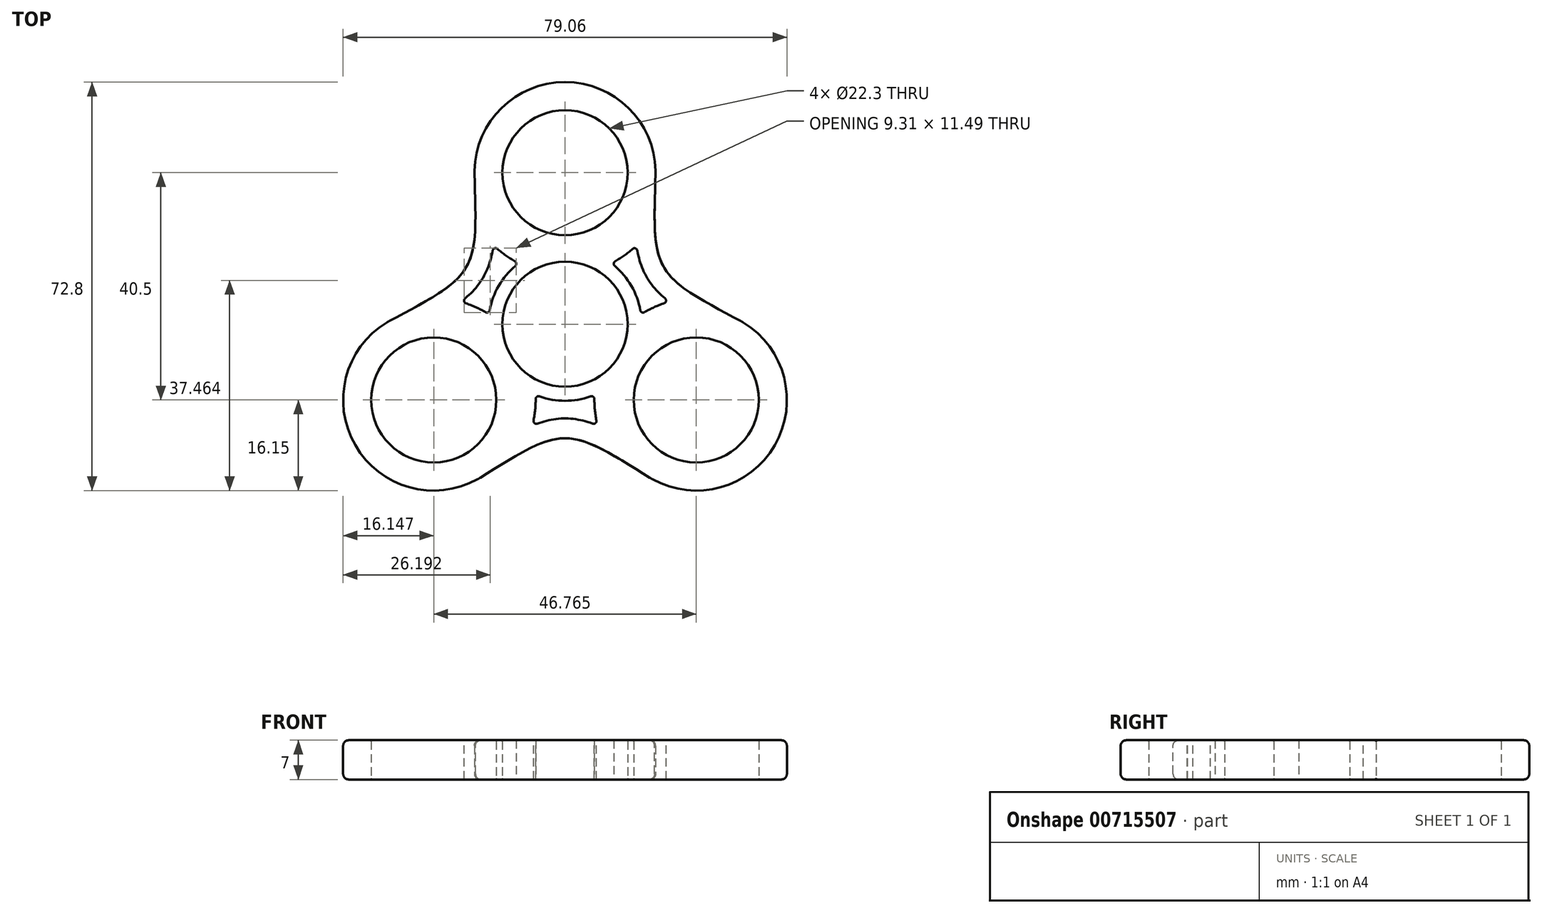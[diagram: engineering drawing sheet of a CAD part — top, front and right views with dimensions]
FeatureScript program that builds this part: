
annotation { "Feature Type Name" : "Feature", "Feature Type Description" : "" }
export const myFeature = defineFeature(function(context is Context, id is Id, definition is map)
    precondition{}
    {
        {
            var Q0;
            Q0=qCreatedBy(makeId("Top.planeOp"),FACE);
            var sketch = newSketch(context, id + "F0", { "sketchPlane" : qUnion([Q0])});
            skCircle(sketch, "E0", {"center": v(0, 0) * mm, "radius": 11.15 * mm});
            skLineSegment(sketch, "E1.0", {"start": v(-15.15, 0) * mm, "end": v(-15.15, 0) * mm});
            skLineSegment(sketch, "E2", {"start": v(0, 0) * mm, "end": v(0, 27) * mm, "construction": true});
            skCircle(sketch, "E3", {"center": v(0, 27) * mm, "radius": 11.15 * mm});
            skArc(sketch, "E4.0", {"start": v(16.15, 27) * mm, "mid": v(0, 43.15) * mm, "end": v(-16.15, 27) * mm});
            skLineSegment(sketch, "E5", {"start": v(-15.15, 0) * mm, "end": v(15.15, 0) * mm, "construction": true});
            skLineSegment(sketch, "E6", {"start": v(-16.15, 27) * mm, "end": v(16.15, 27) * mm, "construction": true});
            skPoint(sketch, "E7.trimOffspring.end.orphan", {"position": v(-15.15, 0) * mm});
            skLineSegment(sketch, "E8", {"start": v(-16.15, 27) * mm, "end": v(-16.15, 27) * mm});
            skArc(sketch, "E9.trimOffspring", {"start": v(-15.15, 0) * mm, "mid": v(0, -15.15) * mm, "end": v(15.15, 0) * mm, "construction": true});
            skLineSegment(sketch, "E10.trimOffspring", {"start": v(16.15, 27) * mm, "end": v(16.15, 27) * mm});
            skLineSegment(sketch, "E11.anchor1", {"start": v(0, 27) * mm, "end": v(0, 43.15) * mm, "construction": true});
            skLineSegment(sketch, "E11.anchor2", {"start": v(0, 27) * mm, "end": v(13.23, 36.26) * mm, "construction": true});
            skLineSegment(sketch, "E12.1.0", {"start": v(7.57, -13.12) * mm, "end": v(-7.58, 13.12) * mm, "construction": true});
            skLineSegment(sketch, "E12.1.2", {"start": v(0, 0) * mm, "end": v(-23.38, -13.5) * mm, "construction": true});
            skLineSegment(sketch, "E12.1.4", {"start": v(-15.3, -27.49) * mm, "end": v(-31.46, 0.49) * mm, "construction": true});
            skCircle(sketch, "E12.1.5", {"center": v(-23.38, -13.5) * mm, "radius": 11.15 * mm});
            skPoint(sketch, "E12.1.9", {"position": v(7.57, -13.12) * mm});
            skArc(sketch, "E12.1.14", {"start": v(-31.46, 0.49) * mm, "mid": v(-37.37, -21.57) * mm, "end": v(-15.3, -27.49) * mm});
            skLineSegment(sketch, "E12.2.0", {"start": v(7.57, 13.12) * mm, "end": v(-7.58, -13.12) * mm, "construction": true});
            skLineSegment(sketch, "E12.2.2", {"start": v(0, 0) * mm, "end": v(23.38, -13.5) * mm, "construction": true});
            skLineSegment(sketch, "E12.2.4", {"start": v(31.46, 0.49) * mm, "end": v(15.3, -27.49) * mm, "construction": true});
            skCircle(sketch, "E12.2.5", {"center": v(23.38, -13.5) * mm, "radius": 11.15 * mm});
            skArc(sketch, "E12.2.12", {"start": v(7.57, 13.12) * mm, "mid": v(-13.12, 7.57) * mm, "end": v(-7.58, -13.12) * mm, "construction": true});
            skArc(sketch, "E12.2.14", {"start": v(15.3, -27.49) * mm, "mid": v(37.37, -21.57) * mm, "end": v(31.46, 0.49) * mm});
            skFitSpline(sketch, "E13", {"points": [v(16.15, 27) * mm, v(31.46, 0.49) * mm], "startDerivative": vector(-1.87, -54.1) * mm, "endDerivative": vector(47.8, -25.43) * mm});
            skLineSegment(sketch, "E14", {"start": v(0, 0) * mm, "end": v(26.97, 15.57) * mm, "construction": true});
            skLineSegment(sketch, "E15", {"start": v(-15.3, -27.49) * mm, "end": v(-3.01, -11.46) * mm});
            skLineSegment(sketch, "E16", {"start": v(-3.01, -11.46) * mm, "end": v(3.36, -11.46) * mm});
            skLineSegment(sketch, "E17", {"start": v(3.36, -11.46) * mm, "end": v(15.3, -27.49) * mm});
            skLineSegment(sketch, "E18", {"start": v(-31.46, 0.49) * mm, "end": v(-13.47, 2.14) * mm});
            skLineSegment(sketch, "E19", {"start": v(-13.47, 2.14) * mm, "end": v(-9.18, 9.2) * mm});
            skLineSegment(sketch, "E20", {"start": v(-9.18, 9.2) * mm, "end": v(-16.15, 27) * mm});
            skSolve(sketch);
        }
        {
            var Q0;
            Q0=qCreatedBy(makeId("Right.planeOp"),FACE);
            var sketch = newSketch(context, id + "F1", { "sketchPlane" : qUnion([Q0])});
            skLineSegment(sketch, "E21", {"start": v(0, 18.91) * mm, "end": v(0, -18.72) * mm, "construction": true});
            skSolve(sketch);
        }
        {
            var Q0;
            Q0=makeQuery(id+"F0.imprint","IMPRINT",FACE,{"disambiguationData":[TD([[makeQuery(id+"F0.imprint","IMPRINT",EDGE,{"derivedFrom":sQuery(id+"F0.wireOp",EDGE,"E0")}),-1.0]])]});
            var Q1;
            Q1=makeQuery(id+"F0.imprint","IMPRINT",FACE,{"disambiguationData":[TD([[makeQuery(id+"F0.imprint","IMPRINT",EDGE,{"derivedFrom":sQuery(id+"F0.wireOp",EDGE,"E3")}),-1.0]])]});
            extrude(context, id + "F2", {"entities" : qUnion([Q0, Q1]), "depth" : 7 * mm, "offsetDistance" : 25 * mm});
        }
        {
            var Q0;
            Q0=makeQuery(id+"F2.opExtrude","SWEPT_BODY",BODY,{"disambiguationData":[OSD([sQuery(id+"F0.wireOp",EDGE,"E0"),sQuery(id+"F0.wireOp",EDGE,"E1.0"),sQuery(id+"F0.wireOp",EDGE,"E3"),sQuery(id+"F0.wireOp",EDGE,"E4.0"),sQuery(id+"F0.wireOp",EDGE,"oIW5whhO-fQ4n-saJ2-gWf4-q0JPziCMkqRt"),sQuery(id+"F0.wireOp",EDGE,"e7664bf7-e720-472f-93c8-efa73fce652a0.MirrorCS"),sQuery(id+"F0.wireOp",EDGE,"15db0cb3-5bd8-46cc-a881-ea2e00802e11.filletArc"),sQuery(id+"F0.wireOp",EDGE,"163ba6b5-26b9-4c58-8659-ca6763b85cf9.filletArc")])]});
            var Q1;
            Q1=sQuery(id+"F1.wireOp",EDGE,"E21");
            circularPattern(context, id + "F3", {"operationType" : NewBodyOperationType.ADD, "entities" : qUnion([Q0]), "axis" : qUnion([Q1]), "angle" : 360 * degree, "instanceCount" : 3, "equalSpace" : true});
        }
        {
            var Q0;
            Q0=makeQuery(id+"F2.opExtrude","SWEPT_EDGE",EDGE,{"disambiguationData":[OSD([sQuery(id+"F0.wireOp",EDGE,"E4.0"),sQuery(id+"F0.wireOp",EDGE,"E13")])]});
            var Q1;
            Q1=makeQuery(id+"F2.opExtrude","SWEPT_EDGE",EDGE,{"disambiguationData":[OSD([sQuery(id+"F0.wireOp",EDGE,"E12.2.14"),sQuery(id+"F0.wireOp",EDGE,"E13")])]});
            var Q2;
            Q2=makeQuery(id+"F3.boolean.opBoolean","MERGE",EDGE,{"derivedFrom":[makeQuery(id+"F2.opExtrude","SWEPT_EDGE",EDGE,{"disambiguationData":[OSD([sQuery(id+"F0.wireOp",EDGE,"E12.2.14"),sQuery(id+"F0.wireOp",EDGE,"E17")])]}),makeQuery(id+"F3.opPattern","COPY",EDGE,{"derivedFrom":makeQuery(id+"F2.opExtrude","SWEPT_EDGE",EDGE,{"disambiguationData":[OSD([sQuery(id+"F0.wireOp",EDGE,"E4.0"),sQuery(id+"F0.wireOp",EDGE,"E13")])]}),"instanceName":"1"})]});
            var Q3;
            Q3=makeQuery(id+"F3.boolean.opBoolean","MERGE",EDGE,{"derivedFrom":[makeQuery(id+"F2.opExtrude","SWEPT_EDGE",EDGE,{"disambiguationData":[OSD([sQuery(id+"F0.wireOp",EDGE,"E12.1.14"),sQuery(id+"F0.wireOp",EDGE,"E15")])]}),makeQuery(id+"F3.opPattern","COPY",EDGE,{"derivedFrom":makeQuery(id+"F2.opExtrude","SWEPT_EDGE",EDGE,{"disambiguationData":[OSD([sQuery(id+"F0.wireOp",EDGE,"E12.2.14"),sQuery(id+"F0.wireOp",EDGE,"E13")])]}),"instanceName":"1"})]});
            var Q4;
            Q4=makeQuery(id+"F3.boolean.opBoolean","MERGE",EDGE,{"derivedFrom":[makeQuery(id+"F2.opExtrude","SWEPT_EDGE",EDGE,{"disambiguationData":[OSD([sQuery(id+"F0.wireOp",EDGE,"E12.1.14"),sQuery(id+"F0.wireOp",EDGE,"E18")])]}),makeQuery(id+"F3.opPattern","COPY",EDGE,{"derivedFrom":makeQuery(id+"F2.opExtrude","SWEPT_EDGE",EDGE,{"disambiguationData":[OSD([sQuery(id+"F0.wireOp",EDGE,"E12.2.14"),sQuery(id+"F0.wireOp",EDGE,"E17")])]}),"instanceName":"1"}),makeQuery(id+"F3.opPattern","COPY",EDGE,{"derivedFrom":makeQuery(id+"F2.opExtrude","SWEPT_EDGE",EDGE,{"disambiguationData":[OSD([sQuery(id+"F0.wireOp",EDGE,"E4.0"),sQuery(id+"F0.wireOp",EDGE,"E13")])]}),"instanceName":"2"})]});
            var Q5;
            Q5=makeQuery(id+"F3.boolean.opBoolean","MERGE",EDGE,{"derivedFrom":[makeQuery(id+"F2.opExtrude","SWEPT_EDGE",EDGE,{"disambiguationData":[OSD([sQuery(id+"F0.wireOp",EDGE,"E4.0"),sQuery(id+"F0.wireOp",EDGE,"E20")])]}),makeQuery(id+"F3.opPattern","COPY",EDGE,{"derivedFrom":makeQuery(id+"F2.opExtrude","SWEPT_EDGE",EDGE,{"disambiguationData":[OSD([sQuery(id+"F0.wireOp",EDGE,"E12.1.14"),sQuery(id+"F0.wireOp",EDGE,"E15")])]}),"instanceName":"1"}),makeQuery(id+"F3.opPattern","COPY",EDGE,{"derivedFrom":makeQuery(id+"F2.opExtrude","SWEPT_EDGE",EDGE,{"disambiguationData":[OSD([sQuery(id+"F0.wireOp",EDGE,"E12.2.14"),sQuery(id+"F0.wireOp",EDGE,"E13")])]}),"instanceName":"2"})]});
            fillet(context, id + "F4", {"entities" : qUnion([Q0, Q1, Q2, Q3, Q4, Q5]), "radius" : 10 * mm, "tangentPropagation" : true, "allowEdgeOverflow" : false});
        }
        {
            var Q0;
            Q0=makeQuery(id+"F2.opExtrude","CAP_EDGE",EDGE,{"disambiguationData":[OSD([sQuery(id+"F0.wireOp",EDGE,"E13")])],"isStart":false});
            var Q1;
            Q1=makeQuery(id+"F3.opPattern","COPY",EDGE,{"derivedFrom":makeQuery(id+"F2.opExtrude","CAP_EDGE",EDGE,{"disambiguationData":[OSD([sQuery(id+"F0.wireOp",EDGE,"E13")])],"isStart":false}),"instanceName":"2"});
            var Q2;
            Q2=makeQuery(id+"F3.opPattern","COPY",EDGE,{"derivedFrom":makeQuery(id+"F2.opExtrude","CAP_EDGE",EDGE,{"disambiguationData":[OSD([sQuery(id+"F0.wireOp",EDGE,"E13")])],"isStart":false}),"instanceName":"1"});
            var Q3;
            Q3=makeQuery(id+"F3.opPattern","COPY",EDGE,{"derivedFrom":makeQuery(id+"F2.opExtrude","CAP_EDGE",EDGE,{"disambiguationData":[OSD([sQuery(id+"F0.wireOp",EDGE,"E13")])],"isStart":true}),"instanceName":"2"});
            var Q4;
            Q4=makeQuery(id+"F2.opExtrude","CAP_EDGE",EDGE,{"disambiguationData":[OSD([sQuery(id+"F0.wireOp",EDGE,"E13")])],"isStart":true});
            fillet(context, id + "F5", {"entities" : qUnion([Q0, Q1, Q2, Q3, Q4]), "radius" : 1 * mm, "tangentPropagation" : true, "allowEdgeOverflow" : false});
        }
        {
            var Q0;
            {var subQ0=makeQuery(id+"F2.opExtrude","CAP_FACE",FACE,{"disambiguationData":[OSD([sQuery(id+"F0.wireOp",EDGE,"E0"),sQuery(id+"F0.wireOp",EDGE,"E3"),sQuery(id+"F0.wireOp",EDGE,"E4.0"),sQuery(id+"F0.wireOp",EDGE,"E12.1.5"),sQuery(id+"F0.wireOp",EDGE,"E12.1.14"),sQuery(id+"F0.wireOp",EDGE,"E12.2.5"),sQuery(id+"F0.wireOp",EDGE,"E12.2.14"),sQuery(id+"F0.wireOp",EDGE,"E13"),sQuery(id+"F0.wireOp",EDGE,"E15"),sQuery(id+"F0.wireOp",EDGE,"E16"),sQuery(id+"F0.wireOp",EDGE,"E17"),sQuery(id+"F0.wireOp",EDGE,"E18"),sQuery(id+"F0.wireOp",EDGE,"E19"),sQuery(id+"F0.wireOp",EDGE,"E20")])],"isStart":false});Q0=makeQuery(id+"F3.boolean.opBoolean","MERGE",FACE,{"derivedFrom":[subQ0,makeQuery(id+"F3.opPattern","COPY",FACE,{"derivedFrom":subQ0,"instanceName":"1"}),makeQuery(id+"F3.opPattern","COPY",FACE,{"derivedFrom":subQ0,"instanceName":"2"})]});}
            var sketch = newSketch(context, id + "F6", { "sketchPlane" : qUnion([Q0])});
            skFitSpline(sketch, "E22.0", {"points": [v(30.8, -0.3) * mm, v(29.52, 0.38) * mm, v(27.61, 1.4) * mm, v(25.08, 2.8) * mm, v(23.2, 3.87) * mm, v(21.38, 5.03) * mm, v(19.92, 6.09) * mm, v(18.81, 7.05) * mm, v(17.78, 8.1) * mm, v(17.02, 9.12) * mm, v(16.5, 10.08) * mm, v(16.17, 10.75) * mm, v(15.84, 11.6) * mm, v(15.54, 12.64) * mm, v(15.25, 14.06) * mm, v(15.05, 15.89) * mm, v(14.96, 18.07) * mm, v(14.96, 20.26) * mm, v(15.02, 23.18) * mm, v(15.1, 25.36) * mm, v(15.14, 26.82) * mm], "construction": true});
            skCircle(sketch, "E23.0", {"center": v(0, 0) * mm, "radius": 11.15 * mm, "construction": true});
            skFitSpline(sketch, "E24.0", {"points": [v(29.62, -2.5) * mm, v(28.99, -2.16) * mm, v(27.7, -1.48) * mm, v(25.79, -0.45) * mm, v(23.86, 0.61) * mm, v(21.92, 1.73) * mm, v(20.31, 2.74) * mm, v(19.02, 3.65) * mm, v(18.06, 4.4) * mm, v(17.1, 5.22) * mm, v(16.18, 6.16) * mm, v(15.33, 7.2) * mm, v(14.59, 8.32) * mm, v(13.95, 9.55) * mm, v(13.47, 10.8) * mm, v(13.11, 12.05) * mm, v(12.77, 13.7) * mm, v(12.55, 15.71) * mm, v(12.46, 18.03) * mm, v(12.46, 20.3) * mm, v(12.52, 23.25) * mm, v(12.6, 25.45) * mm, v(12.64, 26.9) * mm]});
            skCircle(sketch, "E25.0", {"center": v(0, 27) * mm, "radius": 11.15 * mm, "construction": true});
            skCircle(sketch, "E26.0", {"center": v(23.38, -13.5) * mm, "radius": 11.15 * mm, "construction": true});
            skArc(sketch, "E27.0", {"start": v(13.54, 1.75) * mm, "mid": v(11.82, 6.83) * mm, "end": v(8.28, 10.85) * mm});
            skArc(sketch, "E28.0", {"start": v(18.57, 4) * mm, "mid": v(15.97, 3.07) * mm, "end": v(13.54, 1.75) * mm});
            skArc(sketch, "E29.0", {"start": v(8.28, 10.85) * mm, "mid": v(10.64, 12.3) * mm, "end": v(12.75, 14.08) * mm});
            skSolve(sketch);
        }
        {
            var Q0;
            {var subQ0=sQuery(id+"F6.wireOp",EDGE,"E24.0");Q0=makeQuery(id+"F6.imprint","IMPRINT",FACE,{"disambiguationData":[TD([[makeQuery(id+"F6.imprint","IMPRINT",EDGE,{"derivedFrom":subQ0}),1.0]])]});}
            var Q1;
            {var subQ0=makeQuery(id+"F2.opExtrude","CAP_FACE",FACE,{"disambiguationData":[OSD([sQuery(id+"F0.wireOp",EDGE,"E0"),sQuery(id+"F0.wireOp",EDGE,"E3"),sQuery(id+"F0.wireOp",EDGE,"E4.0"),sQuery(id+"F0.wireOp",EDGE,"E12.1.5"),sQuery(id+"F0.wireOp",EDGE,"E12.1.14"),sQuery(id+"F0.wireOp",EDGE,"E12.2.5"),sQuery(id+"F0.wireOp",EDGE,"E12.2.14"),sQuery(id+"F0.wireOp",EDGE,"E13"),sQuery(id+"F0.wireOp",EDGE,"E15"),sQuery(id+"F0.wireOp",EDGE,"E16"),sQuery(id+"F0.wireOp",EDGE,"E17"),sQuery(id+"F0.wireOp",EDGE,"E18"),sQuery(id+"F0.wireOp",EDGE,"E19"),sQuery(id+"F0.wireOp",EDGE,"E20")])],"isStart":true});Q1=makeQuery(id+"F3.boolean.opBoolean","MERGE",FACE,{"derivedFrom":[subQ0,makeQuery(id+"F3.opPattern","COPY",FACE,{"derivedFrom":subQ0,"instanceName":"1"}),makeQuery(id+"F3.opPattern","COPY",FACE,{"derivedFrom":subQ0,"instanceName":"2"})]});}
            extrude(context, id + "F7", {"entities" : qUnion([Q0]), "endBound" : BoundingType.UP_TO_SURFACE, "oppositeDirection" : true, "depth" : 25 * mm, "endBoundEntityFace" : qUnion([Q1]), "offsetDistance" : 25 * mm});
        }
        {
            var Q0;
            Q0=qCreatedBy(makeId("Right.planeOp"),FACE);
            var sketch = newSketch(context, id + "F8", { "sketchPlane" : qUnion([Q0])});
            skLineSegment(sketch, "E30", {"start": v(0, 0) * mm, "end": v(0, 16.42) * mm, "construction": true});
            skSolve(sketch);
        }
        {
            var Q0;
            Q0=makeQuery(id+"F7.opExtrude","SWEPT_BODY",BODY,{"disambiguationData":[OSD([sQuery(id+"F6.wireOp",EDGE,"E24.0"),sQuery(id+"F6.wireOp",EDGE,"E27.0"),sQuery(id+"F6.wireOp",EDGE,"E28.0"),sQuery(id+"F6.wireOp",EDGE,"E29.0")])]});
            var Q1;
            Q1=sQuery(id+"F8.wireOp",EDGE,"E30");
            circularPattern(context, id + "F9", {"operationType" : NewBodyOperationType.REMOVE, "entities" : qUnion([Q0]), "axis" : qUnion([Q1]), "angle" : 360 * degree, "instanceCount" : 3, "equalSpace" : true});
        }
        {
            var Q0;
            Q0=makeQuery(id+"F9.boolean.opBoolean","COPY",EDGE,{"derivedFrom":makeQuery(id+"F9.opPattern","COPY",EDGE,{"derivedFrom":makeQuery(id+"F7.opExtrude","SWEPT_EDGE",EDGE,{"disambiguationData":[OSD([sQuery(id+"F6.wireOp",EDGE,"E27.0"),sQuery(id+"F6.wireOp",EDGE,"E29.0")])]}),"instanceName":"1"})});
            var Q1;
            Q1=makeQuery(id+"F9.boolean.opBoolean","COPY",EDGE,{"derivedFrom":makeQuery(id+"F9.opPattern","COPY",EDGE,{"derivedFrom":makeQuery(id+"F7.opExtrude","SWEPT_EDGE",EDGE,{"disambiguationData":[OSD([sQuery(id+"F6.wireOp",EDGE,"E27.0"),sQuery(id+"F6.wireOp",EDGE,"E28.0")])]}),"instanceName":"1"})});
            var Q2;
            Q2=makeQuery(id+"F9.boolean.opBoolean","COPY",EDGE,{"derivedFrom":makeQuery(id+"F9.opPattern","COPY",EDGE,{"derivedFrom":makeQuery(id+"F7.opExtrude","SWEPT_EDGE",EDGE,{"disambiguationData":[OSD([sQuery(id+"F6.wireOp",EDGE,"E24.0"),sQuery(id+"F6.wireOp",EDGE,"E29.0")])]}),"instanceName":"1"})});
            var Q3;
            Q3=makeQuery(id+"F9.boolean.opBoolean","COPY",EDGE,{"derivedFrom":makeQuery(id+"F9.opPattern","COPY",EDGE,{"derivedFrom":makeQuery(id+"F7.opExtrude","SWEPT_EDGE",EDGE,{"disambiguationData":[OSD([sQuery(id+"F6.wireOp",EDGE,"E24.0"),sQuery(id+"F6.wireOp",EDGE,"E28.0")])]}),"instanceName":"1"})});
            var Q4;
            Q4=makeQuery(id+"F9.boolean.opBoolean","COPY",EDGE,{"derivedFrom":makeQuery(id+"F7.opExtrude","SWEPT_EDGE",EDGE,{"disambiguationData":[OSD([sQuery(id+"F6.wireOp",EDGE,"E27.0"),sQuery(id+"F6.wireOp",EDGE,"E29.0")])]})});
            var Q5;
            Q5=makeQuery(id+"F9.boolean.opBoolean","COPY",EDGE,{"derivedFrom":makeQuery(id+"F7.opExtrude","SWEPT_EDGE",EDGE,{"disambiguationData":[OSD([sQuery(id+"F6.wireOp",EDGE,"E24.0"),sQuery(id+"F6.wireOp",EDGE,"E29.0")])]})});
            var Q6;
            Q6=makeQuery(id+"F9.boolean.opBoolean","COPY",EDGE,{"derivedFrom":makeQuery(id+"F7.opExtrude","SWEPT_EDGE",EDGE,{"disambiguationData":[OSD([sQuery(id+"F6.wireOp",EDGE,"E27.0"),sQuery(id+"F6.wireOp",EDGE,"E28.0")])]})});
            var Q7;
            Q7=makeQuery(id+"F9.boolean.opBoolean","COPY",EDGE,{"derivedFrom":makeQuery(id+"F7.opExtrude","SWEPT_EDGE",EDGE,{"disambiguationData":[OSD([sQuery(id+"F6.wireOp",EDGE,"E24.0"),sQuery(id+"F6.wireOp",EDGE,"E28.0")])]})});
            var Q8;
            Q8=makeQuery(id+"F9.boolean.opBoolean","COPY",EDGE,{"derivedFrom":makeQuery(id+"F9.opPattern","COPY",EDGE,{"derivedFrom":makeQuery(id+"F7.opExtrude","SWEPT_EDGE",EDGE,{"disambiguationData":[OSD([sQuery(id+"F6.wireOp",EDGE,"E27.0"),sQuery(id+"F6.wireOp",EDGE,"E29.0")])]}),"instanceName":"2"})});
            var Q9;
            Q9=makeQuery(id+"F9.boolean.opBoolean","COPY",EDGE,{"derivedFrom":makeQuery(id+"F9.opPattern","COPY",EDGE,{"derivedFrom":makeQuery(id+"F7.opExtrude","SWEPT_EDGE",EDGE,{"disambiguationData":[OSD([sQuery(id+"F6.wireOp",EDGE,"E27.0"),sQuery(id+"F6.wireOp",EDGE,"E28.0")])]}),"instanceName":"2"})});
            var Q10;
            Q10=makeQuery(id+"F9.boolean.opBoolean","COPY",EDGE,{"derivedFrom":makeQuery(id+"F9.opPattern","COPY",EDGE,{"derivedFrom":makeQuery(id+"F7.opExtrude","SWEPT_EDGE",EDGE,{"disambiguationData":[OSD([sQuery(id+"F6.wireOp",EDGE,"E24.0"),sQuery(id+"F6.wireOp",EDGE,"E28.0")])]}),"instanceName":"2"})});
            var Q11;
            Q11=makeQuery(id+"F9.boolean.opBoolean","COPY",EDGE,{"derivedFrom":makeQuery(id+"F9.opPattern","COPY",EDGE,{"derivedFrom":makeQuery(id+"F7.opExtrude","SWEPT_EDGE",EDGE,{"disambiguationData":[OSD([sQuery(id+"F6.wireOp",EDGE,"E24.0"),sQuery(id+"F6.wireOp",EDGE,"E29.0")])]}),"instanceName":"2"})});
            fillet(context, id + "F10", {"entities" : qUnion([Q0, Q1, Q2, Q3, Q4, Q5, Q6, Q7, Q8, Q9, Q10, Q11]), "radius" : 0.5 * mm, "tangentPropagation" : true, "allowEdgeOverflow" : false});
        }
        {
            var Q0;
            Q0=makeQuery(id+"F2.opExtrude","SWEPT_FACE",FACE,{"disambiguationData":[OSD([sQuery(id+"F0.wireOp",EDGE,"E0")])]});
            var Q1;
            Q1=makeQuery(id+"F2.opExtrude","SWEPT_FACE",FACE,{"disambiguationData":[OSD([sQuery(id+"F0.wireOp",EDGE,"E12.2.5")])]});
            var Q2;
            Q2=makeQuery(id+"F2.opExtrude","SWEPT_FACE",FACE,{"disambiguationData":[OSD([sQuery(id+"F0.wireOp",EDGE,"E12.1.5")])]});
            var Q3;
            Q3=makeQuery(id+"F2.opExtrude","SWEPT_FACE",FACE,{"disambiguationData":[OSD([sQuery(id+"F0.wireOp",EDGE,"E3")])]});
            var Q4;
            Q4=makeQuery(id+"F9.boolean.opBoolean","COPY",EDGE,{"derivedFrom":makeQuery(id+"F9.opPattern","COPY",EDGE,{"derivedFrom":makeQuery(id+"F7.opExtrude","CAP_EDGE",EDGE,{"disambiguationData":[OSD([sQuery(id+"F6.wireOp",EDGE,"E27.0")])],"isStart":true}),"instanceName":"1"})});
            var Q5;
            Q5=makeQuery(id+"F9.boolean.opBoolean","COPY",EDGE,{"derivedFrom":makeQuery(id+"F7.opExtrude","CAP_EDGE",EDGE,{"disambiguationData":[OSD([sQuery(id+"F6.wireOp",EDGE,"E27.0")])],"isStart":true})});
            var Q6;
            Q6=makeQuery(id+"F9.boolean.opBoolean","COPY",EDGE,{"derivedFrom":makeQuery(id+"F9.opPattern","COPY",EDGE,{"derivedFrom":makeQuery(id+"F7.opExtrude","CAP_EDGE",EDGE,{"disambiguationData":[OSD([sQuery(id+"F6.wireOp",EDGE,"E24.0")])],"isStart":true}),"instanceName":"2"})});
            var Q7;
            Q7=makeQuery(id+"F9.boolean.opBoolean","COPY",EDGE,{"derivedFrom":makeQuery(id+"F9.opPattern","COPY",EDGE,{"derivedFrom":makeQuery(id+"F7.opExtrude","CAP_EDGE",EDGE,{"disambiguationData":[OSD([sQuery(id+"F6.wireOp",EDGE,"E24.0")])],"isStart":false}),"instanceName":"2"})});
            var Q8;
            Q8=makeQuery(id+"F9.boolean.opBoolean","COPY",EDGE,{"derivedFrom":makeQuery(id+"F9.opPattern","COPY",EDGE,{"derivedFrom":makeQuery(id+"F7.opExtrude","CAP_EDGE",EDGE,{"disambiguationData":[OSD([sQuery(id+"F6.wireOp",EDGE,"E27.0")])],"isStart":false}),"instanceName":"1"})});
            var Q9;
            Q9=makeQuery(id+"F9.boolean.opBoolean","COPY",EDGE,{"derivedFrom":makeQuery(id+"F7.opExtrude","CAP_EDGE",EDGE,{"disambiguationData":[OSD([sQuery(id+"F6.wireOp",EDGE,"E27.0")])],"isStart":false})});
            fillet(context, id + "F11", {"entities" : qUnion([Q0, Q1, Q2, Q3, Q4, Q5, Q6, Q7, Q8, Q9]), "radius" : 0.2 * mm, "tangentPropagation" : true, "allowEdgeOverflow" : false});
        }
    });
